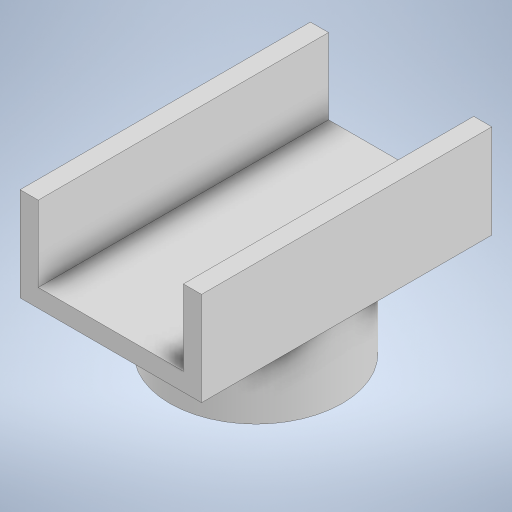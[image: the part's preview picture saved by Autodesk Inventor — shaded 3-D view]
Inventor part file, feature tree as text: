
AUTODESK INVENTOR PART (.ipt)
format: ipt  version: 2024 (Build 280153000, 153)  size: 238,080 bytes
history: native  units: mm
features: extrude x3, other x1, sketch x1, projected_geometry x1
ambient origin geometry x8: Origin, YZ Plane, XZ Plane, XY Plane, X Axis, Y Axis, Z Axis, Center Point
bodies: Body1 (feature_tree)
feature tree (6):
  other  "솔리드1"
  extrude  "돌출1"  Depth=4.8mm
  extrude  "돌출2"  Depth=9.6mm
  extrude  "돌출5"  Depth=0.6mm TaperAngle=0.0deg
  sketch  "스케치2"
  projected_geometry  "투영된 루프1"
